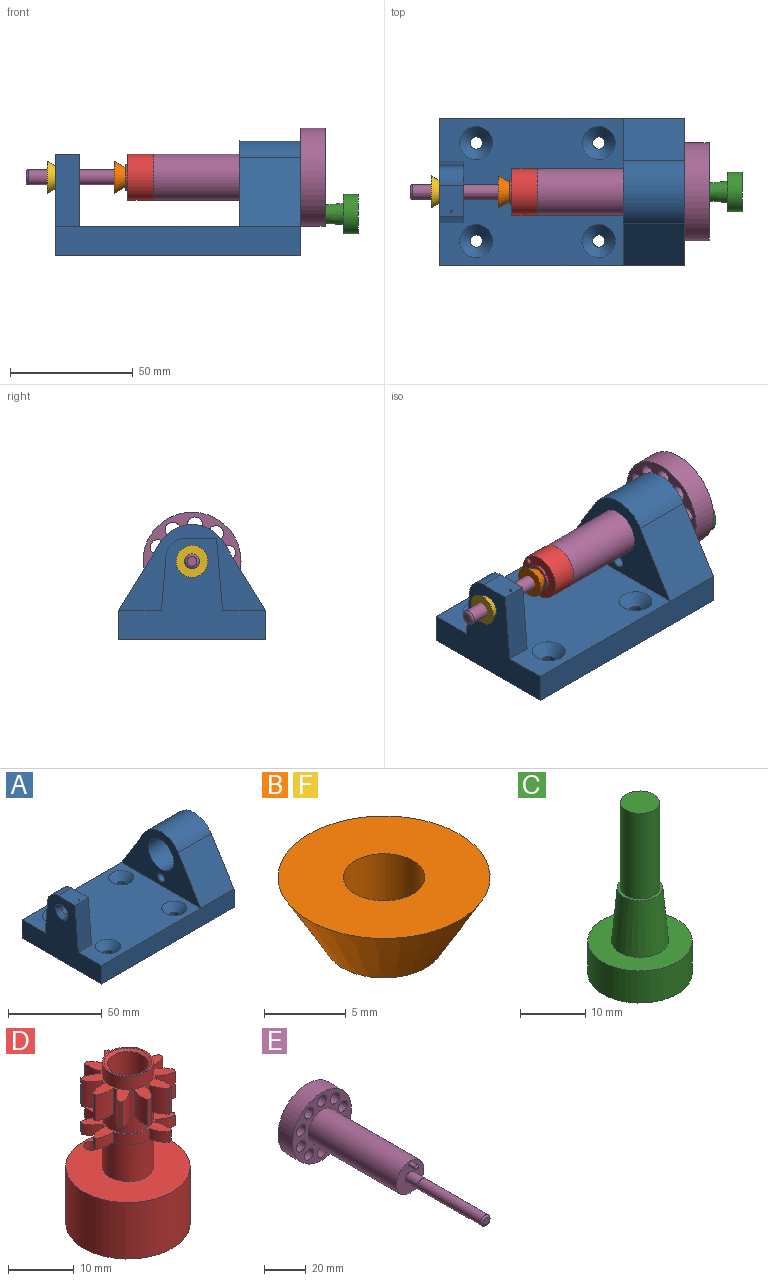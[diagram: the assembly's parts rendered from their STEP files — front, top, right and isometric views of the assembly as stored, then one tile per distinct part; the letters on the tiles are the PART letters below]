
ASSEMBLY  parts=6 mates=5
PART A: 29 faces, bbox 100x60x47 mm
  f0: plane 75x60mm, normal (0,0,1), area 3682.5mm2, adj f1,f3,f4,f11,f13,f15,f17,f19
  f1: plane 100x12mm, normal (0,-1,0), area 1200mm2, adj f0,f2,f4,f5,f6
  f2: plane 60x47mm, normal (1,0,0), area 1740.5mm2, adj f1,f3,f5,f6,f7,f8,f9,f10
  f3: plane 100x12mm, normal (0,1,0), area 1200mm2, adj f0,f2,f4,f5,f7
  f4: plane 60x41.45mm, normal (-1,0,0), area 1301mm2, adj f0,f1,f3,f5,f20,f21,f22,f24
  f5: plane 100x60mm, normal (0,0,-1), area 5921.5mm2, adj f1,f2,f3,f4,f12,f14,f16,f18
  f6: plane 27.89x25mm, normal (0,-0.85,0.53), area 819.7mm2, adj f1,f2,f9,f11
  f7: plane 27.89x25mm, normal (0,0.85,0.53), area 819.7mm2, adj f2,f3,f9,f11
  f8: cylinder r=9.45mm len=25mm, axis (1,0,0), area 1484.4mm2, adj f2,f11
  f9: cylinder r=15mm len=25.52mm, axis (1,0,0), area 762.8mm2, adj f2,f6,f7,f11
  f10: cylinder r=2.5mm len=25mm, axis (1,0,0), area 392.7mm2, adj f2,f11
  f11: plane 60x35mm, normal (-1,0,0), area 1020.5mm2, adj f0,f6,f7,f8,f9,f10
  f12: cylinder r=2.5mm len=7.78mm, axis (0,0,1), area 122.2mm2, adj f5,f13
  f13: cone r=2.5mm half-angle=45deg, axis (0,0,1), area 172.9mm2, adj f0,f12
  f14: cylinder r=2.5mm len=7.78mm, axis (0,0,1), area 122.2mm2, adj f5,f15
  f15: cone r=2.5mm half-angle=45deg, axis (0,0,1), area 172.9mm2, adj f0,f14
  f16: cylinder r=2.5mm len=7.78mm, axis (0,0,1), area 122.2mm2, adj f5,f17
  f17: cone r=2.5mm half-angle=45deg, axis (0,0,1), area 172.9mm2, adj f0,f16
  f18: cylinder r=2.5mm len=7.78mm, axis (0,0,1), area 122.2mm2, adj f5,f19
  f19: cone r=2.5mm half-angle=45deg, axis (0,0,1), area 172.9mm2, adj f0,f18
  f20: plane 22.13x10mm, normal (0,1,0.08), area 222.1mm2, adj f0,f4,f24,f25
  f21: plane 29.45x10mm, normal (0,-1,0.08), area 295.6mm2, adj f0,f4,f22,f25
  f22: plane 12.65x10mm, normal (0,0,1), area 125.7mm2, adj f4,f21,f24,f25,f26
  f23: cylinder r=3mm len=7mm, axis (-1,0,0), area 131.9mm2, adj f25,f28
  f24: cylinder r=8mm len=10mm, axis (-1,0,0), area 118.9mm2, adj f4,f20,f22,f25
  f25: plane 29.45x25mm, normal (1,0,0), area 623.1mm2, adj f0,f20,f21,f22,f23,f24
  f26: cylinder r=0.5mm len=5mm, axis (0,0,1), area 15.7mm2, adj f22,f27
  f27: plane 1x1mm, normal (0,0,1), area 0.8mm2, adj f26
  f28: cone r=3mm half-angle=30deg, axis (-1,0,0), area 84.1mm2, adj f4,f23
PART B: 4 faces, bbox 13x13x5 mm
  f0: plane 7.23x7.23mm, normal (0,0,-1), area 21.4mm2, adj f1,f3
  f1: cylinder r=2.5mm len=5mm, axis (0,0,1), area 78.5mm2, adj f0,f2
  f2: plane 13x13mm, normal (0,0,1), area 113.1mm2, adj f1,f3
  f3: cone r=6.5mm half-angle=30deg, axis (0,0,1), area 183.4mm2, adj f0,f2
PART C: 7 faces, bbox 16x16x32 mm
  f0: plane 6x6mm, normal (0,0,1), area 28.3mm2, adj f1
  f1: cylinder r=3mm len=16mm, axis (0,0,1), area 301.6mm2, adj f0,f2
  f2: plane 7x7mm, normal (0,0,1), area 10.2mm2, adj f1,f3
  f3: cone r=4.37mm half-angle=5deg, axis (0,0,-1), area 248.3mm2, adj f2,f6
  f4: cylinder r=8mm len=16mm, axis (0,0,1), area 301.6mm2, adj f5,f6
  f5: plane 16x16mm, normal (0,0,-1), area 201.1mm2, adj f4
  f6: plane 16x16mm, normal (0,0,1), area 140.9mm2, adj f3,f4
PART D: 89 faces, bbox 18.9x18.9x30.9 mm
  f0: cylinder r=3.9mm len=7.8mm, axis (0,0,-1), area 58.8mm2, adj f9,f87
  f1: cylinder r=3.9mm len=7.8mm, axis (0,0,-1), area 80.9mm2, adj f13,f88
  f2: cone r=3.12mm half-angle=30deg, axis (0,0,-1), area 49.7mm2, adj f3,f10
  f3: plane 10.5x10.5mm, normal (0,0,-1), area 31.2mm2, adj f2,f4
  f4: cylinder r=5.25mm len=10.5mm, axis (0,0,-1), area 29.7mm2, adj f3,f5
  f5: plane 18.9x18.9mm, normal (0,0,-1), area 189.4mm2, adj f4,f6,f11
  f6: cylinder r=9.45mm len=18.9mm, axis (0,0,-1), area 623.4mm2, adj f5,f7
  f7: plane 18.9x18.9mm, normal (0,0,1), area 228.2mm2, adj f6,f8,f11
  f8: cylinder r=3.9mm len=7.8mm, axis (0,0,-1), area 172.8mm2, adj f7,f14
  f9: plane 7.8x7.8mm, normal (0,0,1), area 6.2mm2, adj f0,f12
  f10: cylinder r=3.12mm len=28.73mm, axis (0,0,-1), area 563.2mm2, adj f2,f12
  f11: cylinder r=1.2mm len=10.5mm, axis (0,0,1), area 79.2mm2, adj f5,f7
  f12: cone r=3.64mm half-angle=60deg, axis (0,0,1), area 12.7mm2, adj f9,f10
  f13: plane 14.4x13.88mm, normal (0,0,1), area 46.7mm2, adj f1,f15,f16,f17,f18,f19,f20,f21
  f14: plane 14.4x13.88mm, normal (0,0,-1), area 46.7mm2, adj f8,f15,f16,f17,f18,f19,f20,f21
  f15: cylinder r=4.2mm len=1.95mm, axis (0,0,-1), area 1.6mm2, adj f13,f14,f16,f17
  f16: cylinder r=4.5mm len=2.3mm, axis (0,0,-1), area 6.3mm2, adj f13,f14,f15,f21
  f17: cylinder r=4.5mm len=3.09mm, axis (0,0,-1), area 6.3mm2, adj f13,f14,f15,f46
  f18: cylinder r=4.5mm len=2.85mm, axis (0,0,-1), area 6.3mm2, adj f13,f14,f19,f21
  f19: cylinder r=4.2mm len=1.95mm, axis (0,0,-1), area 1.6mm2, adj f13,f14,f18,f20
  f20: cylinder r=4.5mm len=3.12mm, axis (0,0,-1), area 6.3mm2, adj f13,f14,f19,f25
  f21: cylinder r=7.2mm len=1.95mm, axis (0,0,-1), area 1.2mm2, adj f13,f14,f16,f18
  f22: cylinder r=4.5mm len=2.76mm, axis (0,0,-1), area 6.3mm2, adj f13,f14,f23,f25
  f23: cylinder r=4.2mm len=1.95mm, axis (0,0,-1), area 1.6mm2, adj f13,f14,f22,f24
  f24: cylinder r=4.5mm len=2.76mm, axis (0,0,-1), area 6.3mm2, adj f13,f14,f23,f29
  f25: cylinder r=7.2mm len=1.95mm, axis (0,0,-1), area 1.2mm2, adj f13,f14,f20,f22
  f26: cylinder r=4.5mm len=3.12mm, axis (0,0,-1), area 6.3mm2, adj f13,f14,f27,f29
  f27: cylinder r=4.2mm len=1.95mm, axis (0,0,-1), area 1.6mm2, adj f13,f14,f26,f28
  f28: cylinder r=4.5mm len=2.85mm, axis (0,0,-1), area 6.3mm2, adj f13,f14,f27,f33
  f29: cylinder r=7.2mm len=1.95mm, axis (0,0,-1), area 1.2mm2, adj f13,f14,f24,f26
  f30: cylinder r=4.5mm len=2.3mm, axis (0,0,-1), area 6.3mm2, adj f13,f14,f31,f33
  f31: cylinder r=4.2mm len=1.95mm, axis (0,0,-1), area 1.6mm2, adj f13,f14,f30,f32
  f32: cylinder r=4.5mm len=3.09mm, axis (0,0,-1), area 6.3mm2, adj f13,f14,f31,f37
  f33: cylinder r=7.2mm len=1.95mm, axis (0,0,-1), area 1.2mm2, adj f13,f14,f28,f30
  f34: cylinder r=4.5mm len=3.09mm, axis (0,0,-1), area 6.3mm2, adj f13,f14,f35,f37
  f35: cylinder r=4.2mm len=1.95mm, axis (0,0,-1), area 1.6mm2, adj f13,f14,f34,f36
  f36: cylinder r=4.5mm len=2.3mm, axis (0,0,-1), area 6.3mm2, adj f13,f14,f35,f41
  f37: cylinder r=7.2mm len=1.95mm, axis (0,0,-1), area 1.2mm2, adj f13,f14,f32,f34
  f38: cylinder r=4.5mm len=2.85mm, axis (0,0,-1), area 6.3mm2, adj f13,f14,f39,f41
  f39: cylinder r=4.2mm len=1.95mm, axis (0,0,-1), area 1.6mm2, adj f13,f14,f38,f40
  f40: cylinder r=4.5mm len=3.12mm, axis (0,0,-1), area 6.3mm2, adj f13,f14,f39,f44
  f41: cylinder r=7.2mm len=1.95mm, axis (0,0,-1), area 1.2mm2, adj f13,f14,f36,f38
  f42: cylinder r=4.5mm len=2.76mm, axis (0,0,-1), area 6.3mm2, adj f13,f14,f43,f44
  f43: cylinder r=4.2mm len=4.5mm, axis (0,0,-1), area 11.9mm2, adj f13,f14,f42,f45
  f44: cylinder r=7.2mm len=1.95mm, axis (0,0,-1), area 1.2mm2, adj f13,f14,f40,f42
  f45: cylinder r=4.5mm len=3.09mm, axis (0,0,-1), area 6.3mm2, adj f13,f14,f43,f46
  f46: cylinder r=7.2mm len=1.95mm, axis (0,0,-1), area 1.2mm2, adj f13,f14,f17,f45
  f47: cylinder r=4.5mm len=4.8mm, axis (0,0,-1), area 15.4mm2, adj f48,f86,f87,f88
  f48: cylinder r=7.2mm len=4.8mm, axis (0,0,-1), area 3.1mm2, adj f47,f49,f87,f88
  f49: cylinder r=4.5mm len=4.8mm, axis (0,0,-1), area 15.4mm2, adj f48,f50,f87,f88
  f50: cylinder r=4.2mm len=4.8mm, axis (0,0,-1), area 3.9mm2, adj f49,f51,f87,f88
  f51: cylinder r=4.5mm len=4.8mm, axis (0,0,-1), area 15.4mm2, adj f50,f52,f87,f88
  f52: cylinder r=7.2mm len=4.8mm, axis (0,0,-1), area 3.1mm2, adj f51,f53,f87,f88
  f53: cylinder r=4.5mm len=4.8mm, axis (0,0,-1), area 15.4mm2, adj f52,f54,f87,f88
  f54: cylinder r=4.2mm len=4.8mm, axis (0,0,-1), area 3.9mm2, adj f53,f55,f87,f88
  f55: cylinder r=4.5mm len=4.8mm, axis (0,0,-1), area 15.4mm2, adj f54,f56,f87,f88
  f56: cylinder r=7.2mm len=4.8mm, axis (0,0,-1), area 3.1mm2, adj f55,f57,f87,f88
  f57: cylinder r=4.5mm len=4.8mm, axis (0,0,-1), area 15.4mm2, adj f56,f58,f87,f88
  f58: cylinder r=4.2mm len=4.8mm, axis (0,0,-1), area 3.9mm2, adj f57,f59,f87,f88
  f59: cylinder r=4.5mm len=4.8mm, axis (0,0,-1), area 15.4mm2, adj f58,f60,f87,f88
  f60: cylinder r=7.2mm len=4.8mm, axis (0,0,-1), area 3.1mm2, adj f59,f61,f87,f88
  f61: cylinder r=4.5mm len=4.8mm, axis (0,0,-1), area 15.4mm2, adj f60,f62,f87,f88
  f62: cylinder r=4.2mm len=4.8mm, axis (0,0,-1), area 3.9mm2, adj f61,f63,f87,f88
  f63: cylinder r=4.5mm len=4.8mm, axis (0,0,-1), area 15.4mm2, adj f62,f64,f87,f88
  f64: cylinder r=7.2mm len=4.8mm, axis (0,0,-1), area 3.1mm2, adj f63,f65,f87,f88
  f65: cylinder r=4.5mm len=4.8mm, axis (0,0,-1), area 15.4mm2, adj f64,f66,f87,f88
  f66: cylinder r=4.2mm len=4.8mm, axis (0,0,-1), area 3.9mm2, adj f65,f67,f87,f88
  f67: cylinder r=4.5mm len=4.8mm, axis (0,0,-1), area 15.4mm2, adj f66,f68,f87,f88
  f68: cylinder r=7.2mm len=4.8mm, axis (0,0,-1), area 3.1mm2, adj f67,f69,f87,f88
  f69: cylinder r=4.5mm len=4.8mm, axis (0,0,-1), area 15.4mm2, adj f68,f70,f87,f88
  f70: cylinder r=4.2mm len=4.8mm, axis (0,0,-1), area 3.9mm2, adj f69,f71,f87,f88
  f71: cylinder r=4.5mm len=4.8mm, axis (0,0,-1), area 15.4mm2, adj f70,f72,f87,f88
  f72: cylinder r=7.2mm len=4.8mm, axis (0,0,-1), area 3.1mm2, adj f71,f73,f87,f88
  f73: cylinder r=4.5mm len=4.8mm, axis (0,0,-1), area 15.4mm2, adj f72,f74,f87,f88
  f74: cylinder r=4.2mm len=4.8mm, axis (0,0,-1), area 3.9mm2, adj f73,f75,f87,f88
  f75: cylinder r=4.5mm len=4.8mm, axis (0,0,-1), area 15.4mm2, adj f74,f76,f87,f88
  f76: cylinder r=7.2mm len=4.8mm, axis (0,0,-1), area 3.1mm2, adj f75,f77,f87,f88
  f77: cylinder r=4.5mm len=4.8mm, axis (0,0,-1), area 15.4mm2, adj f76,f78,f87,f88
  f78: cylinder r=4.2mm len=4.8mm, axis (0,0,-1), area 3.9mm2, adj f77,f79,f87,f88
  f79: cylinder r=4.5mm len=4.8mm, axis (0,0,-1), area 15.4mm2, adj f78,f80,f87,f88
  f80: cylinder r=7.2mm len=4.8mm, axis (0,0,-1), area 3.1mm2, adj f79,f81,f87,f88
  f81: cylinder r=4.5mm len=4.8mm, axis (0,0,-1), area 15.4mm2, adj f80,f82,f87,f88
  f82: cylinder r=4.2mm len=4.8mm, axis (0,0,-1), area 3.9mm2, adj f81,f83,f87,f88
  f83: cylinder r=4.5mm len=4.8mm, axis (0,0,-1), area 15.4mm2, adj f82,f84,f87,f88
  f84: cylinder r=7.2mm len=4.8mm, axis (0,0,-1), area 3.1mm2, adj f83,f85,f87,f88
  f85: cylinder r=4.5mm len=4.8mm, axis (0,0,-1), area 15.4mm2, adj f84,f86,f87,f88
  f86: cylinder r=4.2mm len=4.8mm, axis (0,0,-1), area 3.9mm2, adj f47,f85,f87,f88
  f87: plane 14.4x13.88mm, normal (0,0,1), area 56.4mm2, adj f0,f47,f48,f49,f50,f51,f52,f53
  f88: plane 14.4x13.88mm, normal (0,0,-1), area 56.4mm2, adj f1,f47,f48,f49,f50,f51,f52,f53
PART E: 23 faces, bbox 40x122x40 mm
  f0: cylinder r=20mm len=40mm, axis (0,1,0), area 1256.6mm2, adj f1,f2
  f1: plane 40x40mm, normal (0,-1,0), area 669.3mm2, adj f0,f3,f4,f5,f6,f7,f8,f9
  f2: plane 40x40mm, normal (0,1,0), area 754mm2, adj f0,f3,f4,f5,f6,f7,f8,f9
  f3: cone r=4mm half-angle=5deg, axis (0,1,0), area 224.7mm2, adj f1,f2
  f4: cone r=4mm half-angle=5deg, axis (0,1,0), area 224.7mm2, adj f1,f2
  f5: cone r=4mm half-angle=5deg, axis (0,1,0), area 224.7mm2, adj f1,f2
  f6: cone r=4mm half-angle=5deg, axis (0,1,0), area 224.7mm2, adj f1,f2
  f7: cone r=4mm half-angle=5deg, axis (0,1,0), area 224.7mm2, adj f1,f2
  f8: cone r=4mm half-angle=5deg, axis (0,1,0), area 224.7mm2, adj f1,f2
  f9: cone r=4mm half-angle=5deg, axis (0,1,0), area 224.7mm2, adj f1,f2
  f10: cone r=4mm half-angle=5deg, axis (0,1,0), area 224.7mm2, adj f1,f2
  f11: cone r=4mm half-angle=5deg, axis (0,1,0), area 224.7mm2, adj f1,f2
  f12: cone r=4mm half-angle=5deg, axis (0,1,0), area 224.7mm2, adj f1,f2
  f13: cylinder r=9.45mm len=60mm, axis (0,1,0), area 3562.6mm2, adj f1,f14
  f14: plane 18.9x18.9mm, normal (0,-1,0), area 245.8mm2, adj f13,f15,f19
  f15: cylinder r=3.1mm len=8mm, axis (0,1,0), area 155.8mm2, adj f14,f16
  f16: plane 6.2x6.2mm, normal (0,-1,0), area 1.9mm2, adj f15,f18
  f17: plane 4x4mm, normal (0,-1,0), area 12.6mm2, adj f22
  f18: cylinder r=3mm len=43mm, axis (0,1,0), area 810.5mm2, adj f16,f22
  f19: cylinder r=1.2mm len=4mm, axis (0,1,0), area 30.2mm2, adj f14,f21
  f20: plane 0.4x0.4mm, normal (0,-1,0), area 0.1mm2, adj f21
  f21: torus R=0.2mm, axis (0,-1,0), area 8.3mm2, adj f19,f20
  f22: torus R=2mm, axis (0,-1,0), area 26mm2, adj f17,f18
PART F: same geometry as B
PLACE A at identity fixed
PLACE B rot(axis=(0.71,-0.03,-0.71),176.6deg) t=(-20.99,0,32)mm
PLACE C rot(axis=(0.71,0,-0.71),180deg) t=(67.42,0,17)mm
PLACE D rot(axis=(0.33,0.89,0.33),96.9deg) t=(-21.4,0,32)mm
PLACE E rot(axis=(-0.68,-0.68,-0.25),151.7deg) t=(60,0,32)mm
PLACE F rot(axis=(-0.68,-0.25,0.68),151.7deg) t=(-48.34,0,32)mm
MATE cylindrical B.f1 <-> E.f18  axis (1,0,0) through (-20.99,0,32)mm
MATE slider C.f1 <-> A.f10  axis (-1,0,0) through (41.42,0,17)mm
MATE fastened D.f0 <-> E.f15  axis (-1,0,0) through (-10,0,32)mm
MATE slider F.f1 <-> E.f18  axis (1,0,0) through (-48.34,0,32)mm
MATE revolute E.f13 <-> A.f8  axis (1,0,0) through (50,0,32)mm
